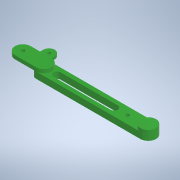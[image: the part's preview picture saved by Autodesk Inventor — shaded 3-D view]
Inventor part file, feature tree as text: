
AUTODESK INVENTOR PART (.ipt)
format: ipt  version: 2021 (Build 250183000, 183)  size: 173,568 bytes
history: native  units: mm
features: extrude x4, sketch x3, projected_geometry x2, other x1
ambient origin geometry x8: Origin, YZ Plane, XZ Plane, XY Plane, X Axis, Y Axis, Z Axis, Center Point
bodies: Body1 (feature_tree)
feature tree (10):
  other  "Sólido1"
  sketch  "Boceto1"  dims[d0=15.0mm d3=3.5mm]
  extrude  "Extrusión1"  Depth=3.5mm
  extrude  "Extrusión2"  Depth=7.0mm
  extrude  "Extrusión3"  Depth=3.0mm
  extrude  "Extrusión4"  Depth=3.0mm
  sketch  "Boceto2"  dims[d5=7.0mm d7=7.0mm]
  projected_geometry  "Contorno proyectado1"
  sketch  "Boceto3"  dims[d10=100.0mm d12=55.0mm d13=55.0mm d18=9.0mm d19=0.0mm d20=6.0mm d21=0.0mm d22=15.0mm d24=3.5mm d25=15.0mm d26=20.0mm d27=20.0mm d28=3.5mm d29=0.0mm d32=3.0mm d35=2.5mm d36=0.0mm d37=6.0mm d38=3.0mm d39=3.0mm]
  projected_geometry  "Contorno proyectado2"
